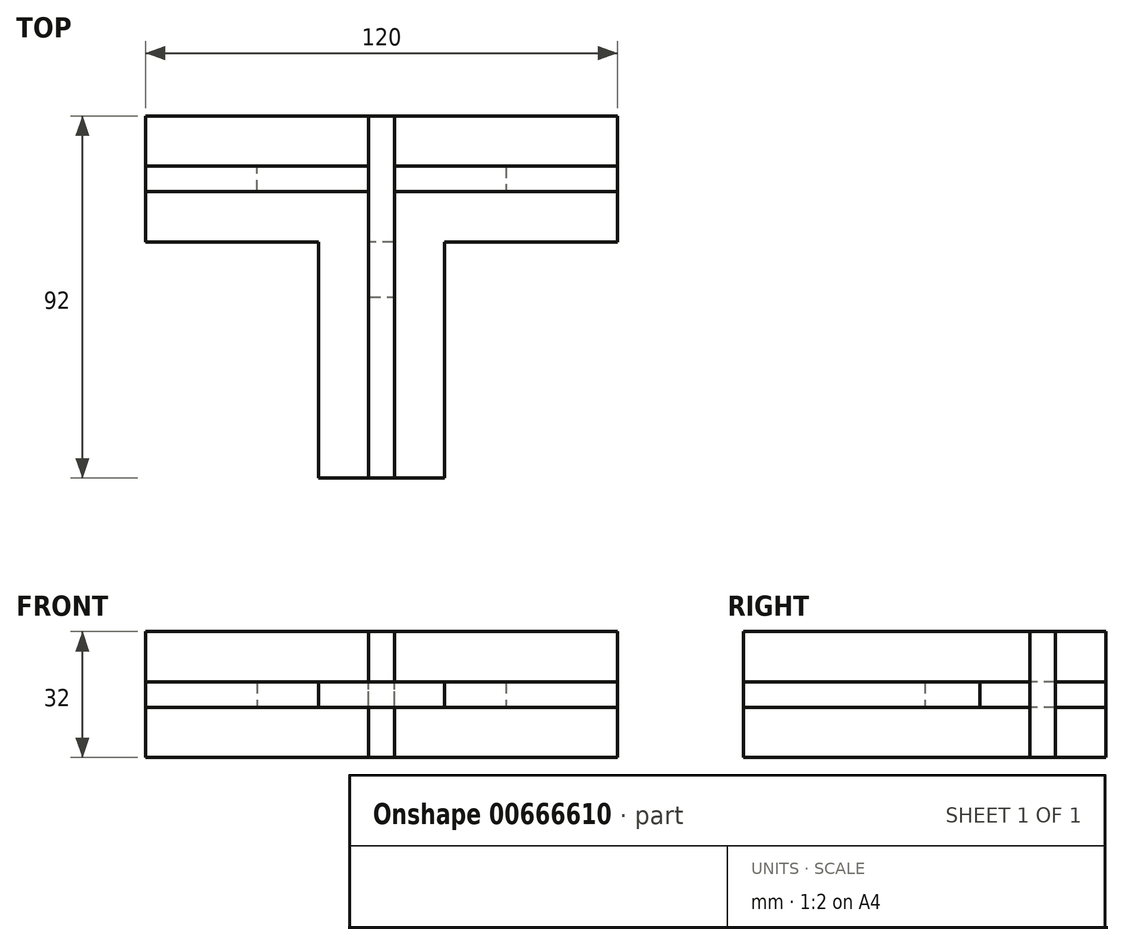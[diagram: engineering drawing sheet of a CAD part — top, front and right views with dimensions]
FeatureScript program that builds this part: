
annotation { "Feature Type Name" : "Feature", "Feature Type Description" : "" }
export const myFeature = defineFeature(function(context is Context, id is Id, definition is map)
    precondition{}
    {
        {
            var Q0;
            Q0=qCreatedBy(makeId("Top.planeOp"),FACE);
            var sketch = newSketch(context, id + "F0", { "sketchPlane" : qUnion([Q0])});
            skLineSegment(sketch, "E0.bottom", {"start": v(60, -16) * mm, "end": v(16, -16) * mm});
            skLineSegment(sketch, "E0.top", {"start": v(60, 16) * mm, "end": v(3.25, 16) * mm});
            skLineSegment(sketch, "E0.left", {"start": v(60, -16) * mm, "end": v(60, -3.25) * mm});
            skLineSegment(sketch, "E0.right", {"start": v(-60, -16) * mm, "end": v(-60, -3.25) * mm});
            skPoint(sketch, "E0.middle", {"position": v(0, 0) * mm});
            skLineSegment(sketch, "E1.top", {"start": v(16, -76) * mm, "end": v(-16, -76) * mm});
            skLineSegment(sketch, "E1.left", {"start": v(16, -16) * mm, "end": v(16, -76) * mm});
            skLineSegment(sketch, "E1.right", {"start": v(-16, -16) * mm, "end": v(-16, -76) * mm});
            skPoint(sketch, "E1.middle", {"position": v(0, -46) * mm});
            skLineSegment(sketch, "E2.trimOffspring", {"start": v(-16, -16) * mm, "end": v(-60, -16) * mm});
            skLineSegment(sketch, "E3.top", {"start": v(-3.25, -30) * mm, "end": v(3.25, -30) * mm});
            skLineSegment(sketch, "E3.left", {"start": v(-3.25, 16) * mm, "end": v(-3.25, -30) * mm});
            skLineSegment(sketch, "E3.right", {"start": v(3.25, 16) * mm, "end": v(3.25, -30) * mm});
            skLineSegment(sketch, "E4.trimOffspring", {"start": v(-3.25, 16) * mm, "end": v(-60, 16) * mm});
            skLineSegment(sketch, "E5", {"start": v(60, 16) * mm, "end": v(60, 3.25) * mm, "construction": true});
            skLineSegment(sketch, "E6.bottom", {"start": v(60, 16) * mm, "end": v(-60, 16) * mm, "construction": true});
            skLineSegment(sketch, "E6.top", {"start": v(60, -16) * mm, "end": v(-60, -16) * mm, "construction": true});
            skLineSegment(sketch, "E6.right", {"start": v(-60, 16) * mm, "end": v(-60, 3.25) * mm, "construction": true});
            skLineSegment(sketch, "E7.bottom", {"start": v(16, -16) * mm, "end": v(-16, -16) * mm, "construction": true});
            skLineSegment(sketch, "E7.top", {"start": v(16, -76) * mm, "end": v(-16, -76) * mm, "construction": true});
            skLineSegment(sketch, "E7.left", {"start": v(16, -16) * mm, "end": v(16, -76) * mm, "construction": true});
            skLineSegment(sketch, "E7.right", {"start": v(-16, -16) * mm, "end": v(-16, -76) * mm, "construction": true});
            skLineSegment(sketch, "E8.bottom", {"start": v(60, 3.25) * mm, "end": v(31.62, 3.25) * mm});
            skLineSegment(sketch, "E8.top", {"start": v(60, -3.25) * mm, "end": v(31.62, -3.25) * mm});
            skLineSegment(sketch, "E8.right", {"start": v(31.62, 3.25) * mm, "end": v(31.62, -3.25) * mm});
            skLineSegment(sketch, "E9.trimOffspring", {"start": v(60, -3.25) * mm, "end": v(60, -16) * mm, "construction": true});
            skLineSegment(sketch, "E10.trimOffspring", {"start": v(60, 3.25) * mm, "end": v(60, 16) * mm});
            skLineSegment(sketch, "E11.bottom", {"start": v(-60, 3.25) * mm, "end": v(-31.63, 3.25) * mm});
            skLineSegment(sketch, "E11.top", {"start": v(-60, -3.25) * mm, "end": v(-31.63, -3.25) * mm});
            skLineSegment(sketch, "E11.right", {"start": v(-31.63, 3.25) * mm, "end": v(-31.63, -3.25) * mm});
            skLineSegment(sketch, "E12.trimOffspring", {"start": v(-60, -3.25) * mm, "end": v(-60, -16) * mm, "construction": true});
            skLineSegment(sketch, "E13.trimOffspring", {"start": v(-60, 3.25) * mm, "end": v(-60, 16) * mm});
            skSolve(sketch);
        }
        {
            var Q0;
            Q0 = qSketchRegion(id + "F0", true);
            extrude(context, id + "F1", {"entities" : qUnion([Q0]), "depth" : 6.5 * mm, "offsetDistance" : 25 * mm});
        }
        {
            var Q0;
            Q0=makeQuery(id+"F1.opExtrude","SWEPT_FACE",FACE,{"disambiguationData":[OSD([sQuery(id+"F0.wireOp",EDGE,"E1.left")])]});
            var sketch = newSketch(context, id + "F2", { "sketchPlane" : qUnion([Q0])});
            skLineSegment(sketch, "E14.bottom", {"start": v(-76, -12.75) * mm, "end": v(16, -12.75) * mm});
            skLineSegment(sketch, "E14.top", {"start": v(-76, 19.25) * mm, "end": v(16, 19.25) * mm});
            skLineSegment(sketch, "E14.left", {"start": v(-76, -12.99) * mm, "end": v(-76, 19.25) * mm});
            skLineSegment(sketch, "E14.right", {"start": v(16, -12.75) * mm, "end": v(16, 19.25) * mm});
            skSolve(sketch);
        }
        {
            var Q0;
            Q0=qCreatedBy(makeId("Right.planeOp"),FACE);
            var sketch = newSketch(context, id + "F3", { "sketchPlane" : qUnion([Q0])});
            skLineSegment(sketch, "E15.bottom", {"start": v(-76, -12.75) * mm, "end": v(16, -12.75) * mm});
            skLineSegment(sketch, "E15.top", {"start": v(-76, 19.25) * mm, "end": v(16, 19.25) * mm});
            skLineSegment(sketch, "E15.left", {"start": v(-76, -12.99) * mm, "end": v(-76, 0) * mm});
            skLineSegment(sketch, "E15.right", {"start": v(16, -12.75) * mm, "end": v(16, 0) * mm});
            skLineSegment(sketch, "E16.right", {"start": v(-16, 0) * mm, "end": v(-16, 6.5) * mm});
            skLineSegment(sketch, "E17.trimOffspring", {"start": v(16, 6.5) * mm, "end": v(16, 19.25) * mm});
            skLineSegment(sketch, "E18.bottom", {"start": v(-16, 6.5) * mm, "end": v(-76, 6.5) * mm});
            skLineSegment(sketch, "E18.top", {"start": v(-16, 0) * mm, "end": v(-76, 0) * mm});
            skLineSegment(sketch, "E18.left", {"start": v(-16, 6.5) * mm, "end": v(-16, 0) * mm});
            skLineSegment(sketch, "E19.trimOffspring", {"start": v(-76, 6.5) * mm, "end": v(-76, 19.25) * mm});
            skLineSegment(sketch, "E20", {"start": v(16, 0) * mm, "end": v(16, 6.5) * mm});
            skSolve(sketch);
        }
        {
            var Q0;
            {var subQ1=sQuery(id+"F3.wireOp",EDGE,"E15.bottom");Q0=makeQuery(id+"F3.imprint","IMPRINT",FACE,{"disambiguationData":[TD([[makeQuery(id+"F3.imprint","IMPRINT",EDGE,{"derivedFrom":subQ1}),1.0]])]});}
            extrude(context, id + "F4", {"entities" : qUnion([Q0]), "endBound" : BoundingType.SYMMETRIC, "depth" : 6.5 * mm, "offsetDistance" : 25 * mm});
        }
        {
            var Q0;
            Q0=makeQuery(id+"F1.opExtrude","SWEPT_FACE",FACE,{"disambiguationData":[OSD([sQuery(id+"F0.wireOp",EDGE,"E8.top")])]});
            cPlane(context, id + "F5", {"entities" : qUnion([Q0]), "cplaneType" : CPlaneType.OFFSET, "offset" : 3.25 * mm, "width" : 150 * mm, "height" : 150 * mm});
        }
        {
            var Q0;
            Q0=qCreatedBy(id+"F5.planeOp",FACE);
            var sketch = newSketch(context, id + "F6", { "sketchPlane" : qUnion([Q0])});
            skLineSegment(sketch, "E21", {"start": v(-31.62, 0) * mm, "end": v(-3.25, 0) * mm, "construction": true});
            skLineSegment(sketch, "E22.bottom", {"start": v(-31.62, 0) * mm, "end": v(60, 0) * mm});
            skLineSegment(sketch, "E22.top", {"start": v(-31.62, 6.5) * mm, "end": v(-3.25, 6.5) * mm});
            skLineSegment(sketch, "E23.top", {"start": v(-60, -12.75) * mm, "end": v(-3.25, -12.75) * mm});
            skLineSegment(sketch, "E23.left", {"start": v(-60, 0) * mm, "end": v(-60, -12.75) * mm});
            skLineSegment(sketch, "E24.left", {"start": v(-60, 6.5) * mm, "end": v(-60, 6.5) * mm});
            skLineSegment(sketch, "E24.right", {"start": v(60, 6.5) * mm, "end": v(60, 6.5) * mm});
            skLineSegment(sketch, "E25.top", {"start": v(-60, 19.25) * mm, "end": v(-3.25, 19.25) * mm});
            skLineSegment(sketch, "E25.left", {"start": v(-60, 6.5) * mm, "end": v(-60, 19.25) * mm});
            skLineSegment(sketch, "E26.left", {"start": v(-60, 19.25) * mm, "end": v(-60, 6.5) * mm});
            skLineSegment(sketch, "E26.right", {"start": v(-3.25, 19.25) * mm, "end": v(-3.25, 6.5) * mm});
            skLineSegment(sketch, "E27.top", {"start": v(-31.62, 0) * mm, "end": v(-3.25, 0) * mm});
            skLineSegment(sketch, "E28", {"start": v(-31.62, 25.84) * mm, "end": v(-31.62, -20.92) * mm, "construction": true});
            skLineSegment(sketch, "E29.right", {"start": v(-31.62, 6.5) * mm, "end": v(-31.62, 0) * mm});
            skPoint(sketch, "E23.right.end.orphan", {"position": v(60, -12.75) * mm});
            skPoint(sketch, "E25.right.end.orphan", {"position": v(60, 19.25) * mm});
            skPoint(sketch, "E30.orphan", {"position": v(60, 0) * mm});
            skLineSegment(sketch, "E31.trimOffspring", {"start": v(-3.25, 0) * mm, "end": v(-3.25, -12.75) * mm});
            skLineSegment(sketch, "E32", {"start": v(-60, 6.5) * mm, "end": v(-60, 0) * mm});
            skPoint(sketch, "E33.orphan", {"position": v(-60, 0) * mm});
            skSolve(sketch);
        }
        {
            var Q0;
            Q0 = qSketchRegion(id + "F6", true);
            extrude(context, id + "F7", {"entities" : qUnion([Q0]), "endBound" : BoundingType.SYMMETRIC, "depth" : 6.5 * mm, "offsetDistance" : 25 * mm});
        }
        {
            var Q0;
            Q0=makeQuery(id+"F7.opExtrude","SWEPT_BODY",BODY,{"disambiguationData":[OSD([sQuery(id+"F6.wireOp",EDGE,"E25.top"),sQuery(id+"F6.wireOp",EDGE,"E23.top"),sQuery(id+"F6.wireOp",EDGE,"E26.left"),sQuery(id+"F6.wireOp",EDGE,"E26.right"),sQuery(id+"F6.wireOp",EDGE,"E22.top"),sQuery(id+"F6.wireOp",EDGE,"E27.top"),sQuery(id+"F6.wireOp",EDGE,"E29.right"),sQuery(id+"F6.wireOp",EDGE,"E23.left"),sQuery(id+"F6.wireOp",EDGE,"E31.trimOffspring"),sQuery(id+"F6.wireOp",EDGE,"E32")])]});
            var Q1;
            Q1=makeQuery(id+"F7.opExtrude","CAP_EDGE",EDGE,{"disambiguationData":[OSD([sQuery(id+"F6.wireOp",EDGE,"E22.top")])],"isStart":false});
            transform(context, id + "F8", {"entities" : qUnion([Q0]), "transformType" : TransformType.TRANSLATION_DISTANCE, "transformDirection" : qUnion([Q1]), "distance" : 63.25 * mm, "makeCopy" : true});
        }
        {
            var Q0;
            Q0=qCreatedBy(makeId("Right.planeOp"),FACE);
            var sketch = newSketch(context, id + "F9", { "sketchPlane" : qUnion([Q0])});
            skLineSegment(sketch, "E34", {"start": v(0, 48.84) * mm, "end": v(0, -52.32) * mm, "construction": true});
            skSolve(sketch);
        }
        {
            var Q0;
            Q0=makeQuery(id+"F8.opPattern","COPY",BODY,{"derivedFrom":makeQuery(id+"F7.opExtrude","SWEPT_BODY",BODY,{"disambiguationData":[OSD([sQuery(id+"F6.wireOp",EDGE,"E25.top"),sQuery(id+"F6.wireOp",EDGE,"E23.top"),sQuery(id+"F6.wireOp",EDGE,"E26.left"),sQuery(id+"F6.wireOp",EDGE,"E26.right"),sQuery(id+"F6.wireOp",EDGE,"E22.top"),sQuery(id+"F6.wireOp",EDGE,"E27.top"),sQuery(id+"F6.wireOp",EDGE,"E29.right"),sQuery(id+"F6.wireOp",EDGE,"E23.left"),sQuery(id+"F6.wireOp",EDGE,"E31.trimOffspring"),sQuery(id+"F6.wireOp",EDGE,"E32")])]}),"instanceName":"1"});
            var Q1;
            Q1=sQuery(id+"F9.wireOp",EDGE,"E34");
            transform(context, id + "F10", {"entities" : qUnion([Q0]), "transformType" : TransformType.ROTATION, "transformAxis" : qUnion([Q1]), "angle" : 180 * degree, "makeCopy" : false});
        }
        {
            var Q0;
            Q0=makeQuery(id+"F8.opPattern","COPY",BODY,{"derivedFrom":makeQuery(id+"F7.opExtrude","SWEPT_BODY",BODY,{"disambiguationData":[OSD([sQuery(id+"F6.wireOp",EDGE,"E25.top"),sQuery(id+"F6.wireOp",EDGE,"E23.top"),sQuery(id+"F6.wireOp",EDGE,"E26.left"),sQuery(id+"F6.wireOp",EDGE,"E26.right"),sQuery(id+"F6.wireOp",EDGE,"E22.top"),sQuery(id+"F6.wireOp",EDGE,"E27.top"),sQuery(id+"F6.wireOp",EDGE,"E29.right"),sQuery(id+"F6.wireOp",EDGE,"E23.left"),sQuery(id+"F6.wireOp",EDGE,"E31.trimOffspring"),sQuery(id+"F6.wireOp",EDGE,"E32")])]}),"instanceName":"1"});
            var Q1;
            Q1=makeQuery(id+"F7.opExtrude","CAP_EDGE",EDGE,{"disambiguationData":[OSD([sQuery(id+"F6.wireOp",EDGE,"E22.top")])],"isStart":true});
            transform(context, id + "F11", {"entities" : qUnion([Q0]), "transformType" : TransformType.TRANSLATION_3D, "dx" : -63.25 * mm, "dy" : 0 * mm, "dz" : 0 * mm, "makeCopy" : false});
        }
    });
